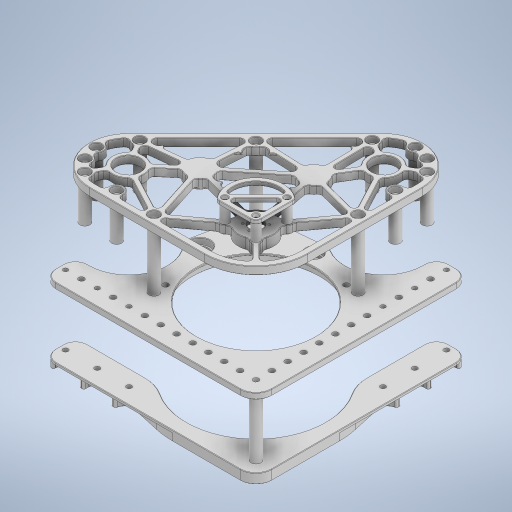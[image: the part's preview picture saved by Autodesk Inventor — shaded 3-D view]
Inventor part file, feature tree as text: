
AUTODESK INVENTOR PART (.ipt)
format: ipt  version: 2023 (Build 270158000, 158)  size: 1,786,368 bytes
history: native  units: in
note: dims shown in document units (in); Inventor stores cm internally (conversion verified against a paired STEP export)
features: other x16, chamfer x3, plane x1
ambient origin geometry x8: Origin, YZ Plane, XZ Plane, XY Plane, X Axis, Y Axis, Z Axis, Center Point
bodies: Solid1 (feature_tree), Solid2 (feature_tree), Solid3 (feature_tree), Solid4 (feature_tree), Solid5 (feature_tree), Solid6 (feature_tree), Solid7 (feature_tree), Solid8 (feature_tree), Solid9 (feature_tree), Solid10 (feature_tree), Solid11 (feature_tree), Solid12 (feature_tree), Solid13 (feature_tree), Solid14 (feature_tree), Solid15 (feature_tree), Solid16 (feature_tree), Solid17 (feature_tree), Solid18 (feature_tree), Solid19 (feature_tree)
feature tree (20):
  plane  "Work Plane1"
  other  "Boss-Extrude4[1]"
  other  "Boss-Extrude4[2]"
  other  "Boss-Extrude4[3]"
  other  "Boss-Extrude6[1]"
  other  "Boss-Extrude6[2]"
  other  "Boss-Extrude6[3]"
  other  "Boss-Extrude6[4]"
  other  "Boss-Extrude6[5]"
  other  "Boss-Extrude6[6]"
  other  "Boss-Extrude6[7]"
  other  "Boss-Extrude6[8]"
  other  "Boss-Extrude9[1]"
  other  "Boss-Extrude17[1]"
  other  "Boss-Extrude17[2]"
  other  "Boss-Extrude17[3]"
  chamfer  "Chamfer4"  [1 undecoded]
  other  "Move Face1"
  chamfer  "Chamfer1"  [1 undecoded]
  chamfer  "Chamfer2"  [1 undecoded]
note: 3 required parameter values undecoded (feature->parameter linkage not recoverable at this tier; creation-order binding heuristic only, values carry confidence <= 0.55)
